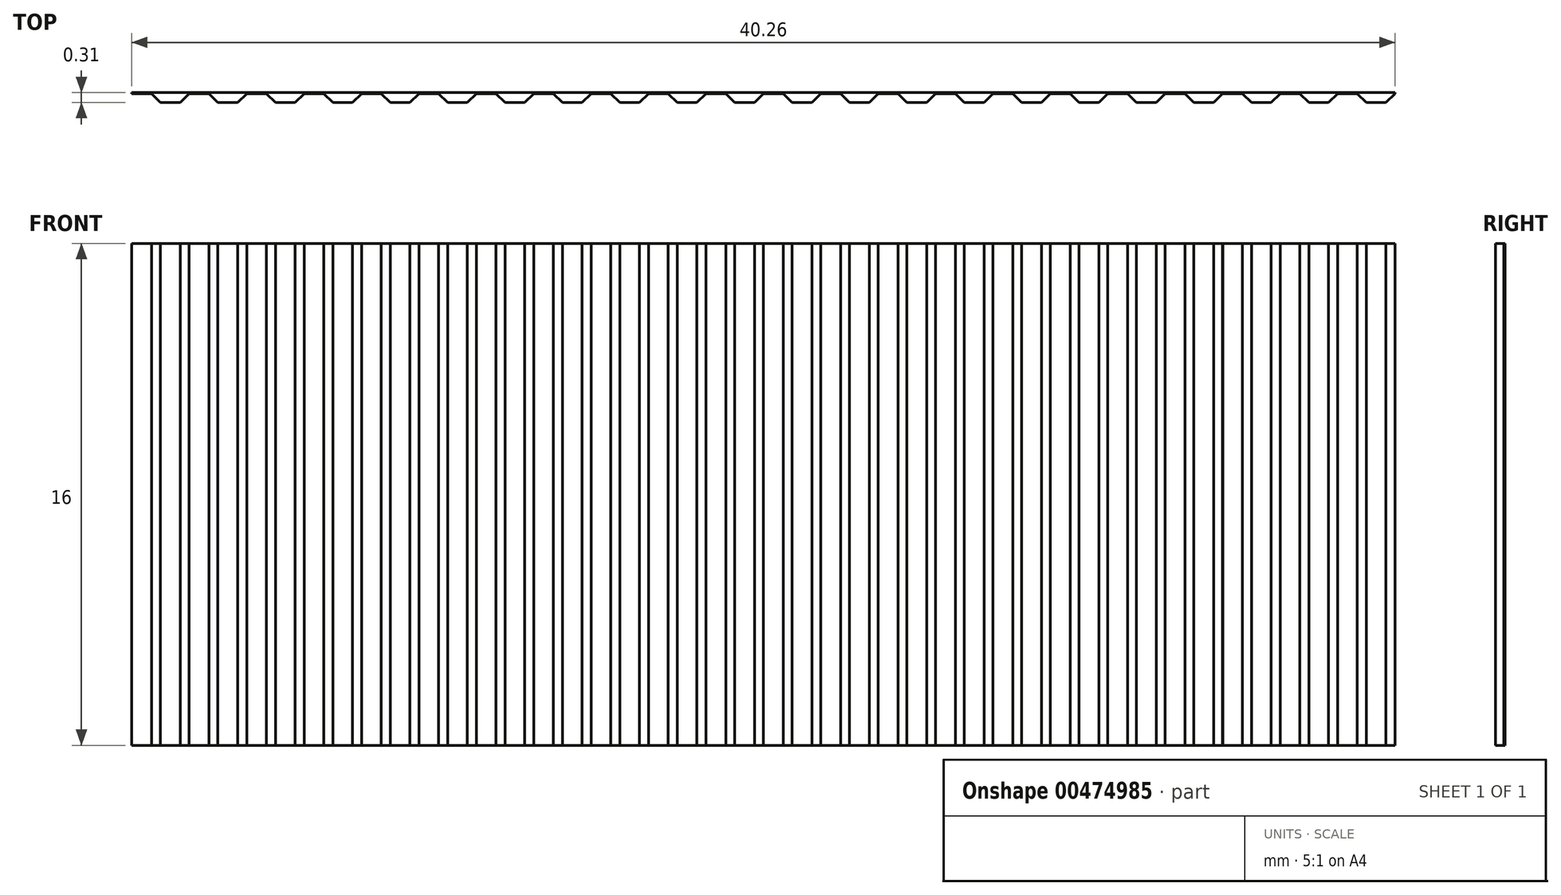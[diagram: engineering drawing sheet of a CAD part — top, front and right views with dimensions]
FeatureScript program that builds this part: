
annotation { "Feature Type Name" : "Feature", "Feature Type Description" : "" }
export const myFeature = defineFeature(function(context is Context, id is Id, definition is map)
    precondition{}
    {
        {
            var Q0;
            Q0=qCreatedBy(makeId("Top.planeOp"),FACE);
            var sketch = newSketch(context, id + "F0", { "sketchPlane" : qUnion([Q0])});
            skLineSegment(sketch, "E0", {"start": v(-1.42, 0.04) * mm, "end": v(0.42, 0.04) * mm});
            skLineSegment(sketch, "E1", {"start": v(-1.41, 0) * mm, "end": v(-0.78, 0) * mm});
            skLineSegment(sketch, "E2", {"start": v(-0.78, 0) * mm, "end": v(-0.5, -0.27) * mm});
            skLineSegment(sketch, "E3", {"start": v(-0.5, -0.27) * mm, "end": v(0.13, -0.27) * mm});
            skLineSegment(sketch, "E4", {"start": v(0.13, -0.27) * mm, "end": v(0.42, 0) * mm});
            skLineSegment(sketch, "E5", {"start": v(-1.42, 0.04) * mm, "end": v(-1.41, 0) * mm});
            skLineSegment(sketch, "E6", {"start": v(0.42, 0.04) * mm, "end": v(0.42, 0) * mm});
            skLineSegment(sketch, "E7", {"start": v(0.41, 0.04) * mm, "end": v(2.25, 0.04) * mm});
            skLineSegment(sketch, "E8", {"start": v(0.42, 0) * mm, "end": v(1.05, 0) * mm});
            skLineSegment(sketch, "E9", {"start": v(1.05, 0) * mm, "end": v(1.33, -0.27) * mm});
            skLineSegment(sketch, "E10", {"start": v(1.33, -0.27) * mm, "end": v(1.96, -0.27) * mm});
            skLineSegment(sketch, "E11", {"start": v(1.96, -0.27) * mm, "end": v(2.25, 0) * mm});
            skLineSegment(sketch, "E12", {"start": v(0.41, 0.04) * mm, "end": v(0.42, 0) * mm});
            skLineSegment(sketch, "E13", {"start": v(2.25, 0.04) * mm, "end": v(2.25, 0) * mm});
            skLineSegment(sketch, "E14", {"start": v(2.24, 0.04) * mm, "end": v(4.08, 0.04) * mm});
            skLineSegment(sketch, "E15", {"start": v(2.25, 0) * mm, "end": v(2.88, 0) * mm});
            skLineSegment(sketch, "E16", {"start": v(2.88, 0) * mm, "end": v(3.16, -0.27) * mm});
            skLineSegment(sketch, "E17", {"start": v(3.16, -0.27) * mm, "end": v(3.8, -0.27) * mm});
            skLineSegment(sketch, "E18", {"start": v(3.8, -0.27) * mm, "end": v(4.08, 0) * mm});
            skLineSegment(sketch, "E19", {"start": v(2.24, 0.04) * mm, "end": v(2.25, 0) * mm});
            skLineSegment(sketch, "E20", {"start": v(4.08, 0.04) * mm, "end": v(4.08, 0) * mm});
            skLineSegment(sketch, "E21", {"start": v(4.07, 0.04) * mm, "end": v(5.9, 0.04) * mm});
            skLineSegment(sketch, "E22", {"start": v(4.08, 0) * mm, "end": v(4.7, 0) * mm});
            skLineSegment(sketch, "E23", {"start": v(4.7, 0) * mm, "end": v(5, -0.27) * mm});
            skLineSegment(sketch, "E24", {"start": v(5, -0.27) * mm, "end": v(5.62, -0.27) * mm});
            skLineSegment(sketch, "E25", {"start": v(5.62, -0.27) * mm, "end": v(5.9, 0) * mm});
            skLineSegment(sketch, "E26", {"start": v(4.07, 0.04) * mm, "end": v(4.08, 0) * mm});
            skLineSegment(sketch, "E27", {"start": v(5.9, 0.04) * mm, "end": v(5.9, 0) * mm});
            skLineSegment(sketch, "E28", {"start": v(5.9, 0.04) * mm, "end": v(7.74, 0.04) * mm});
            skLineSegment(sketch, "E29", {"start": v(5.9, 0) * mm, "end": v(6.54, 0) * mm});
            skLineSegment(sketch, "E30", {"start": v(6.54, 0) * mm, "end": v(6.82, -0.27) * mm});
            skLineSegment(sketch, "E31", {"start": v(6.82, -0.27) * mm, "end": v(7.45, -0.27) * mm});
            skLineSegment(sketch, "E32", {"start": v(7.45, -0.27) * mm, "end": v(7.74, 0) * mm});
            skLineSegment(sketch, "E33", {"start": v(7.74, 0.04) * mm, "end": v(7.74, 0) * mm});
            skLineSegment(sketch, "E34", {"start": v(7.73, 0.04) * mm, "end": v(9.57, 0.04) * mm});
            skLineSegment(sketch, "E35", {"start": v(7.74, 0) * mm, "end": v(8.37, 0) * mm});
            skLineSegment(sketch, "E36", {"start": v(8.37, 0) * mm, "end": v(8.65, -0.27) * mm});
            skLineSegment(sketch, "E37", {"start": v(8.65, -0.27) * mm, "end": v(9.28, -0.27) * mm});
            skLineSegment(sketch, "E38", {"start": v(9.28, -0.27) * mm, "end": v(9.56, 0) * mm});
            skLineSegment(sketch, "E39", {"start": v(7.73, 0.04) * mm, "end": v(7.74, 0) * mm});
            skLineSegment(sketch, "E40", {"start": v(9.57, 0.04) * mm, "end": v(9.56, 0) * mm});
            skLineSegment(sketch, "E41", {"start": v(9.56, 0.04) * mm, "end": v(11.4, 0.04) * mm});
            skLineSegment(sketch, "E42", {"start": v(9.56, 0) * mm, "end": v(10.2, 0) * mm});
            skLineSegment(sketch, "E43", {"start": v(10.2, 0) * mm, "end": v(10.48, -0.27) * mm});
            skLineSegment(sketch, "E44", {"start": v(10.48, -0.27) * mm, "end": v(11.1, -0.27) * mm});
            skLineSegment(sketch, "E45", {"start": v(11.1, -0.27) * mm, "end": v(11.4, 0) * mm});
            skLineSegment(sketch, "E46", {"start": v(9.56, 0.04) * mm, "end": v(9.56, 0) * mm});
            skLineSegment(sketch, "E47", {"start": v(11.4, 0.04) * mm, "end": v(11.4, 0) * mm});
            skLineSegment(sketch, "E48", {"start": v(11.4, 0.04) * mm, "end": v(13.23, 0.04) * mm});
            skLineSegment(sketch, "E49", {"start": v(11.4, 0) * mm, "end": v(12.02, 0) * mm});
            skLineSegment(sketch, "E50", {"start": v(12.02, 0) * mm, "end": v(12.3, -0.27) * mm});
            skLineSegment(sketch, "E51", {"start": v(12.3, -0.27) * mm, "end": v(12.94, -0.27) * mm});
            skLineSegment(sketch, "E52", {"start": v(12.94, -0.27) * mm, "end": v(13.22, 0) * mm});
            skLineSegment(sketch, "E53", {"start": v(13.23, 0.04) * mm, "end": v(13.22, 0) * mm});
            skLineSegment(sketch, "E54", {"start": v(13.22, 0.04) * mm, "end": v(15.06, 0.04) * mm});
            skLineSegment(sketch, "E55", {"start": v(13.22, 0) * mm, "end": v(13.85, 0) * mm});
            skLineSegment(sketch, "E56", {"start": v(13.85, 0) * mm, "end": v(14.14, -0.27) * mm});
            skLineSegment(sketch, "E57", {"start": v(14.14, -0.27) * mm, "end": v(14.77, -0.27) * mm});
            skLineSegment(sketch, "E58", {"start": v(14.77, -0.27) * mm, "end": v(15.05, 0) * mm});
            skLineSegment(sketch, "E59", {"start": v(13.22, 0.04) * mm, "end": v(13.22, 0) * mm});
            skLineSegment(sketch, "E60", {"start": v(15.06, 0.04) * mm, "end": v(15.05, 0) * mm});
            skLineSegment(sketch, "E61", {"start": v(15.05, 0.04) * mm, "end": v(16.89, 0.04) * mm});
            skLineSegment(sketch, "E62", {"start": v(15.05, 0) * mm, "end": v(15.68, 0) * mm});
            skLineSegment(sketch, "E63", {"start": v(15.68, 0) * mm, "end": v(15.97, -0.27) * mm});
            skLineSegment(sketch, "E64", {"start": v(15.97, -0.27) * mm, "end": v(16.6, -0.27) * mm});
            skLineSegment(sketch, "E65", {"start": v(16.6, -0.27) * mm, "end": v(16.88, 0) * mm});
            skLineSegment(sketch, "E66", {"start": v(15.05, 0.04) * mm, "end": v(15.05, 0) * mm});
            skLineSegment(sketch, "E67", {"start": v(16.89, 0.04) * mm, "end": v(16.88, 0) * mm});
            skLineSegment(sketch, "E68", {"start": v(16.88, 0.04) * mm, "end": v(18.71, 0.04) * mm});
            skLineSegment(sketch, "E69", {"start": v(16.88, 0) * mm, "end": v(17.51, 0) * mm});
            skLineSegment(sketch, "E70", {"start": v(17.51, 0) * mm, "end": v(17.8, -0.27) * mm});
            skLineSegment(sketch, "E71", {"start": v(17.8, -0.27) * mm, "end": v(18.43, -0.27) * mm});
            skLineSegment(sketch, "E72", {"start": v(18.43, -0.27) * mm, "end": v(18.71, 0) * mm});
            skLineSegment(sketch, "E73", {"start": v(16.88, 0.04) * mm, "end": v(16.88, 0) * mm});
            skLineSegment(sketch, "E74", {"start": v(18.71, 0.04) * mm, "end": v(18.71, 0) * mm});
            skLineSegment(sketch, "E75", {"start": v(18.7, 0.04) * mm, "end": v(20.54, 0.04) * mm});
            skLineSegment(sketch, "E76", {"start": v(18.71, 0) * mm, "end": v(19.34, 0) * mm});
            skLineSegment(sketch, "E77", {"start": v(19.34, 0) * mm, "end": v(19.63, -0.27) * mm});
            skLineSegment(sketch, "E78", {"start": v(19.63, -0.27) * mm, "end": v(20.26, -0.27) * mm});
            skLineSegment(sketch, "E79", {"start": v(20.26, -0.27) * mm, "end": v(20.54, 0) * mm});
            skLineSegment(sketch, "E80", {"start": v(18.7, 0.04) * mm, "end": v(18.71, 0) * mm});
            skLineSegment(sketch, "E81", {"start": v(20.54, 0.04) * mm, "end": v(20.54, 0) * mm});
            skLineSegment(sketch, "E82", {"start": v(20.54, 0.04) * mm, "end": v(22.37, 0.04) * mm});
            skLineSegment(sketch, "E83", {"start": v(20.54, 0) * mm, "end": v(21.17, 0) * mm});
            skLineSegment(sketch, "E84", {"start": v(21.17, 0) * mm, "end": v(21.45, -0.27) * mm});
            skLineSegment(sketch, "E85", {"start": v(21.45, -0.27) * mm, "end": v(22.09, -0.27) * mm});
            skLineSegment(sketch, "E86", {"start": v(22.09, -0.27) * mm, "end": v(22.37, 0) * mm});
            skLineSegment(sketch, "E87", {"start": v(22.37, 0.04) * mm, "end": v(22.37, 0) * mm});
            skLineSegment(sketch, "E88", {"start": v(22.37, 0.04) * mm, "end": v(24.2, 0.04) * mm});
            skLineSegment(sketch, "E89", {"start": v(22.37, 0) * mm, "end": v(23, 0) * mm});
            skLineSegment(sketch, "E90", {"start": v(23, 0) * mm, "end": v(23.28, -0.27) * mm});
            skLineSegment(sketch, "E91", {"start": v(23.28, -0.27) * mm, "end": v(23.92, -0.27) * mm});
            skLineSegment(sketch, "E92", {"start": v(23.92, -0.27) * mm, "end": v(24.2, 0) * mm});
            skLineSegment(sketch, "E93", {"start": v(24.2, 0.04) * mm, "end": v(24.2, 0) * mm});
            skLineSegment(sketch, "E94", {"start": v(24.2, 0.04) * mm, "end": v(26.03, 0.04) * mm});
            skLineSegment(sketch, "E95", {"start": v(24.2, 0) * mm, "end": v(24.83, 0) * mm});
            skLineSegment(sketch, "E96", {"start": v(24.83, 0) * mm, "end": v(25.11, -0.27) * mm});
            skLineSegment(sketch, "E97", {"start": v(25.11, -0.27) * mm, "end": v(25.74, -0.27) * mm});
            skLineSegment(sketch, "E98", {"start": v(25.74, -0.27) * mm, "end": v(26.03, 0) * mm});
            skLineSegment(sketch, "E99", {"start": v(26.03, 0.04) * mm, "end": v(26.03, 0) * mm});
            skLineSegment(sketch, "E100", {"start": v(26.03, 0.04) * mm, "end": v(27.86, 0.04) * mm});
            skLineSegment(sketch, "E101", {"start": v(26.03, 0) * mm, "end": v(26.66, 0) * mm});
            skLineSegment(sketch, "E102", {"start": v(26.66, 0) * mm, "end": v(26.94, -0.27) * mm});
            skLineSegment(sketch, "E103", {"start": v(26.94, -0.27) * mm, "end": v(27.57, -0.27) * mm});
            skLineSegment(sketch, "E104", {"start": v(27.57, -0.27) * mm, "end": v(27.86, 0) * mm});
            skLineSegment(sketch, "E105", {"start": v(27.86, 0.04) * mm, "end": v(27.86, 0) * mm});
            skLineSegment(sketch, "E106", {"start": v(27.86, 0.04) * mm, "end": v(29.7, 0.04) * mm});
            skLineSegment(sketch, "E107", {"start": v(27.86, 0) * mm, "end": v(28.49, 0) * mm});
            skLineSegment(sketch, "E108", {"start": v(28.49, 0) * mm, "end": v(28.77, -0.27) * mm});
            skLineSegment(sketch, "E109", {"start": v(28.77, -0.27) * mm, "end": v(29.4, -0.27) * mm});
            skLineSegment(sketch, "E110", {"start": v(29.4, -0.27) * mm, "end": v(29.69, 0) * mm});
            skLineSegment(sketch, "E111", {"start": v(29.7, 0.04) * mm, "end": v(29.69, 0) * mm});
            skLineSegment(sketch, "E112", {"start": v(29.68, 0.04) * mm, "end": v(31.52, 0.04) * mm});
            skLineSegment(sketch, "E113", {"start": v(29.69, 0) * mm, "end": v(30.32, 0) * mm});
            skLineSegment(sketch, "E114", {"start": v(30.32, 0) * mm, "end": v(30.6, -0.27) * mm});
            skLineSegment(sketch, "E115", {"start": v(30.6, -0.27) * mm, "end": v(31.23, -0.27) * mm});
            skLineSegment(sketch, "E116", {"start": v(31.23, -0.27) * mm, "end": v(31.52, 0) * mm});
            skLineSegment(sketch, "E117", {"start": v(29.68, 0.04) * mm, "end": v(29.69, 0) * mm});
            skLineSegment(sketch, "E118", {"start": v(31.52, 0.04) * mm, "end": v(31.52, 0) * mm});
            skLineSegment(sketch, "E119", {"start": v(31.51, 0.04) * mm, "end": v(33.35, 0.04) * mm});
            skLineSegment(sketch, "E120", {"start": v(31.52, 0) * mm, "end": v(32.15, 0) * mm});
            skLineSegment(sketch, "E121", {"start": v(32.15, 0) * mm, "end": v(32.43, -0.27) * mm});
            skLineSegment(sketch, "E122", {"start": v(32.43, -0.27) * mm, "end": v(33.06, -0.27) * mm});
            skLineSegment(sketch, "E123", {"start": v(33.06, -0.27) * mm, "end": v(33.35, 0) * mm});
            skLineSegment(sketch, "E124", {"start": v(31.51, 0.04) * mm, "end": v(31.52, 0) * mm});
            skLineSegment(sketch, "E125", {"start": v(33.35, 0.04) * mm, "end": v(33.35, 0) * mm});
            skLineSegment(sketch, "E126", {"start": v(33.35, 0.04) * mm, "end": v(35.18, 0.04) * mm});
            skLineSegment(sketch, "E127", {"start": v(33.35, 0) * mm, "end": v(33.98, 0) * mm});
            skLineSegment(sketch, "E128", {"start": v(33.98, 0) * mm, "end": v(34.26, -0.27) * mm});
            skLineSegment(sketch, "E129", {"start": v(34.26, -0.27) * mm, "end": v(34.9, -0.27) * mm});
            skLineSegment(sketch, "E130", {"start": v(34.9, -0.27) * mm, "end": v(35.18, 0) * mm});
            skLineSegment(sketch, "E131", {"start": v(35.18, 0.04) * mm, "end": v(35.18, 0) * mm});
            skLineSegment(sketch, "E132", {"start": v(35.18, 0.04) * mm, "end": v(37.01, 0.04) * mm});
            skLineSegment(sketch, "E133", {"start": v(35.18, 0) * mm, "end": v(35.8, 0) * mm});
            skLineSegment(sketch, "E134", {"start": v(35.8, 0) * mm, "end": v(36.1, -0.27) * mm});
            skLineSegment(sketch, "E135", {"start": v(36.1, -0.27) * mm, "end": v(36.72, -0.27) * mm});
            skLineSegment(sketch, "E136", {"start": v(36.72, -0.27) * mm, "end": v(37, 0) * mm});
            skLineSegment(sketch, "E137", {"start": v(37.01, 0.04) * mm, "end": v(37, 0) * mm});
            skLineSegment(sketch, "E138", {"start": v(37, 0.04) * mm, "end": v(38.84, 0.04) * mm});
            skLineSegment(sketch, "E139", {"start": v(37, 0) * mm, "end": v(37.64, 0) * mm});
            skLineSegment(sketch, "E140", {"start": v(37.64, 0) * mm, "end": v(37.92, -0.27) * mm});
            skLineSegment(sketch, "E141", {"start": v(37.92, -0.27) * mm, "end": v(38.55, -0.27) * mm});
            skLineSegment(sketch, "E142", {"start": v(38.55, -0.27) * mm, "end": v(38.84, 0) * mm});
            skLineSegment(sketch, "E143", {"start": v(37, 0.04) * mm, "end": v(37, 0) * mm});
            skLineSegment(sketch, "E144", {"start": v(38.84, 0.04) * mm, "end": v(38.84, 0) * mm});
            skSolve(sketch);
        }
        {
            var Q0;
            Q0 = qSketchRegion(id + "F0", true);
            extrude(context, id + "F1", {"entities" : qUnion([Q0]), "depth" : 16 * mm});
        }
    });
